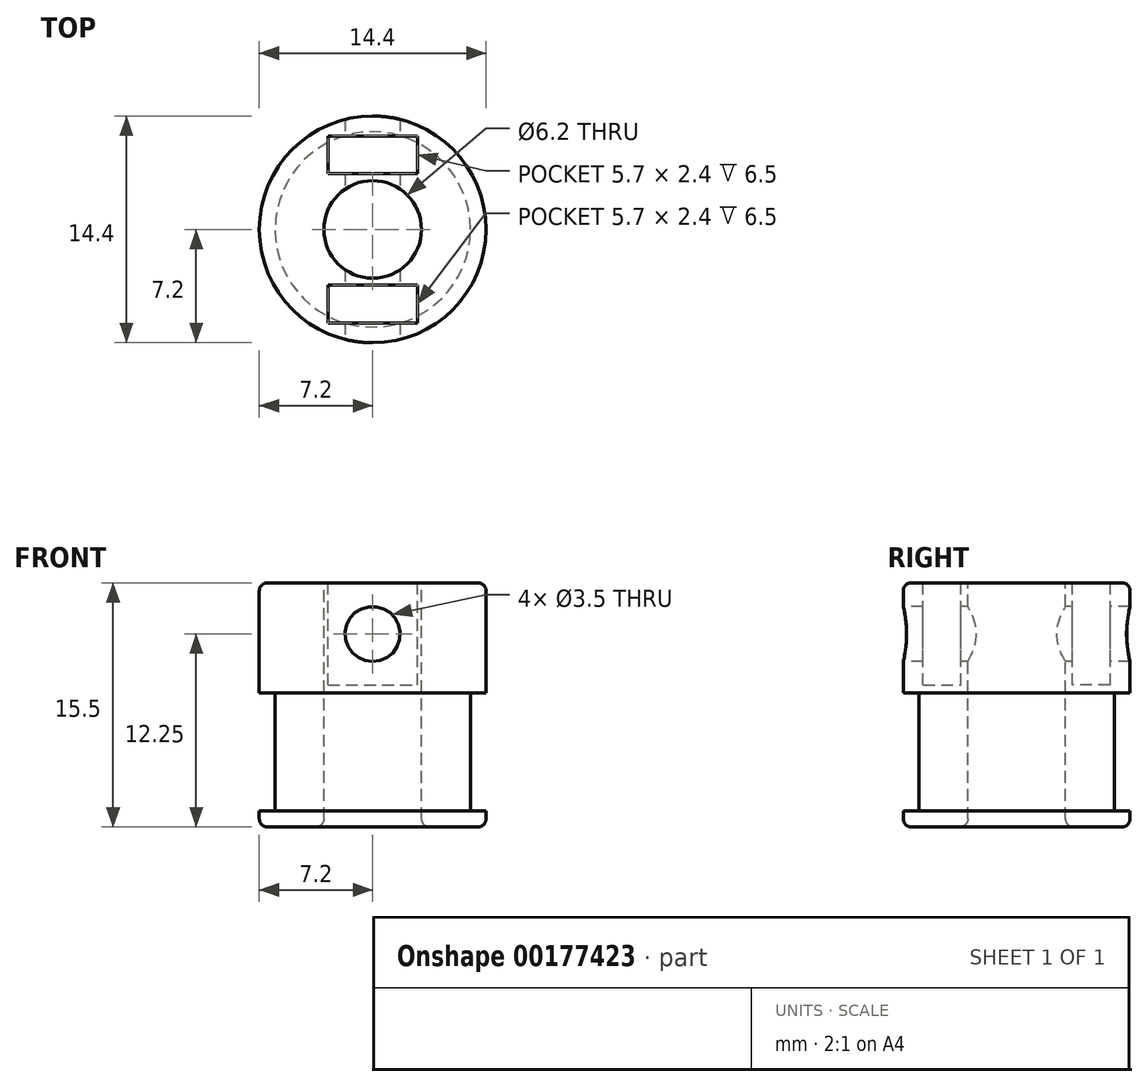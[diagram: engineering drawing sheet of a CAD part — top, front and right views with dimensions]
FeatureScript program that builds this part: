
annotation { "Feature Type Name" : "Feature", "Feature Type Description" : "" }
export const myFeature = defineFeature(function(context is Context, id is Id, definition is map)
    precondition{}
    {
        {
            var Q0;
            Q0=qCreatedBy(makeId("Front.planeOp"),FACE);
            var sketch = newSketch(context, id + "F0", { "sketchPlane" : qUnion([Q0])});
            skLineSegment(sketch, "E0", {"start": v(0, 0) * mm, "end": v(-7.2, 0) * mm});
            skLineSegment(sketch, "E1", {"start": v(-7.2, 15.5) * mm, "end": v(0, 15.5) * mm});
            skLineSegment(sketch, "E2", {"start": v(-7.2, 1) * mm, "end": v(-6.2, 1) * mm});
            skLineSegment(sketch, "E3", {"start": v(-6.2, 1) * mm, "end": v(-6.2, 8.5) * mm});
            skLineSegment(sketch, "E4", {"start": v(-6.2, 8.5) * mm, "end": v(-7.2, 8.5) * mm});
            skLineSegment(sketch, "E5", {"start": v(0, 15.5) * mm, "end": v(0, 0) * mm});
            skLineSegment(sketch, "E6", {"start": v(-3.1, 15.5) * mm, "end": v(-3.1, 0) * mm});
            skLineSegment(sketch, "E7", {"start": v(-7.2, 15.5) * mm, "end": v(-7.2, 8.5) * mm});
            skLineSegment(sketch, "E8", {"start": v(-7.2, 1) * mm, "end": v(-7.2, 0) * mm});
            skCircle(sketch, "E9", {"center": v(-7.2, 6.14) * mm, "radius": 1 * mm, "construction": true});
            skSolve(sketch);
        }
        {
            var Q0;
            {var subQ7=sQuery(id+"F0.wireOp",EDGE,"E2");Q0=makeQuery(id+"F0.imprint","IMPRINT",FACE,{"disambiguationData":[TD([[makeQuery(id+"F0.imprint","IMPRINT",EDGE,{"derivedFrom":subQ7}),-1.0]])]});}
            var Q1;
            Q1=sQuery(id+"F0.wireOp",EDGE,"E5");
            revolve(context, id + "F1", {"entities" : qUnion([Q0]), "axis" : qUnion([Q1]), "revolveType" : RevolveType.FULL});
        }
        {
            var Q0;
            Q0=makeQuery(id+"F1.opRevolve","SWEPT_FACE",FACE,{"disambiguationData":[OSD([sQuery(id+"F0.wireOp",EDGE,"E1")])]});
            var sketch = newSketch(context, id + "F2", { "sketchPlane" : qUnion([Q0])});
            skLineSegment(sketch, "E10.bottom", {"start": v(-2.85, 5.94) * mm, "end": v(2.85, 5.94) * mm});
            skLineSegment(sketch, "E10.top", {"start": v(-2.85, 3.54) * mm, "end": v(2.85, 3.54) * mm});
            skLineSegment(sketch, "E10.left", {"start": v(-2.85, 5.94) * mm, "end": v(-2.85, 3.54) * mm});
            skLineSegment(sketch, "E10.right", {"start": v(2.85, 5.94) * mm, "end": v(2.85, 3.54) * mm});
            skLineSegment(sketch, "E11.MirrorCS", {"start": v(-2.85, -5.94) * mm, "end": v(-2.85, -3.54) * mm});
            skLineSegment(sketch, "E12.MirrorCS", {"start": v(-2.85, -3.54) * mm, "end": v(2.85, -3.54) * mm});
            skLineSegment(sketch, "E13.MirrorCS", {"start": v(-2.85, -5.94) * mm, "end": v(2.85, -5.94) * mm});
            skLineSegment(sketch, "E14.MirrorCS", {"start": v(2.85, -5.94) * mm, "end": v(2.85, -3.54) * mm});
            skSolve(sketch);
        }
        {
            var Q0;
            Q0=makeQuery(id+"F2.imprint","IMPRINT",FACE,{"disambiguationData":[TD([[makeQuery(id+"F2.imprint","IMPRINT",EDGE,{"derivedFrom":sQuery(id+"F2.wireOp",EDGE,"E11.MirrorCS")}),-1.0]])]});
            var Q1;
            Q1=makeQuery(id+"F2.imprint","IMPRINT",FACE,{"disambiguationData":[TD([[makeQuery(id+"F2.imprint","IMPRINT",EDGE,{"derivedFrom":sQuery(id+"F2.wireOp",EDGE,"E10.bottom")}),-1.0]])]});
            extrude(context, id + "F3", {"entities" : qUnion([Q0, Q1]), "operationType" : NewBodyOperationType.REMOVE, "oppositeDirection" : true, "depth" : 6.5 * mm});
        }
        {
            var Q0;
            Q0=makeQuery(id+"F3.boolean.opBoolean","COPY",FACE,{"derivedFrom":makeQuery(id+"F3.opExtrude","SWEPT_FACE",FACE,{"disambiguationData":[OSD([sQuery(id+"F2.wireOp",EDGE,"E12.MirrorCS")])]})});
            var sketch = newSketch(context, id + "F4", { "sketchPlane" : qUnion([Q0])});
            skCircle(sketch, "E15", {"center": v(0, 12.25) * mm, "radius": 1.75 * mm});
            skPoint(sketch, "E15.centerSnap0", {"position": v(-2.85, 12.25) * mm});
            skSolve(sketch);
        }
        {
            var Q0;
            Q0=makeQuery(id+"F4.imprint","IMPRINT",FACE,{"disambiguationData":[TD([[makeQuery(id+"F4.imprint","IMPRINT",EDGE,{"derivedFrom":sQuery(id+"F4.wireOp",EDGE,"E15")}),1.0]])]});
            extrude(context, id + "F5", {"entities" : qUnion([Q0]), "operationType" : NewBodyOperationType.REMOVE, "endBound" : BoundingType.THROUGH_ALL, "oppositeDirection" : true, "depth" : 25 * mm, "hasSecondDirection" : true, "secondDirectionBound" : SecondDirectionBoundingType.THROUGH_ALL, "secondDirectionOppositeDirection" : false, "secondDirectionDepth" : 25 * mm});
        }
        {
            var Q0;
            Q0=makeQuery(id+"F1.opRevolve","SWEPT_EDGE",EDGE,{"disambiguationData":[OSD([sQuery(id+"F0.wireOp",EDGE,"E0"),sQuery(id+"F0.wireOp",EDGE,"E8")])]});
            var Q1;
            Q1=makeQuery(id+"F1.opRevolve","SWEPT_EDGE",EDGE,{"disambiguationData":[OSD([sQuery(id+"F0.wireOp",EDGE,"E1"),sQuery(id+"F0.wireOp",EDGE,"E7")])]});
            var Q2;
            Q2=makeQuery(id+"F1.opRevolve","SWEPT_EDGE",EDGE,{"disambiguationData":[OSD([sQuery(id+"F0.wireOp",EDGE,"E0"),sQuery(id+"F0.wireOp",EDGE,"E6")])]});
            fillet(context, id + "F6", {"entities" : qUnion([Q0, Q1, Q2]), "radius" : 0.5 * mm, "tangentPropagation" : true, "allowEdgeOverflow" : false});
        }
    });
